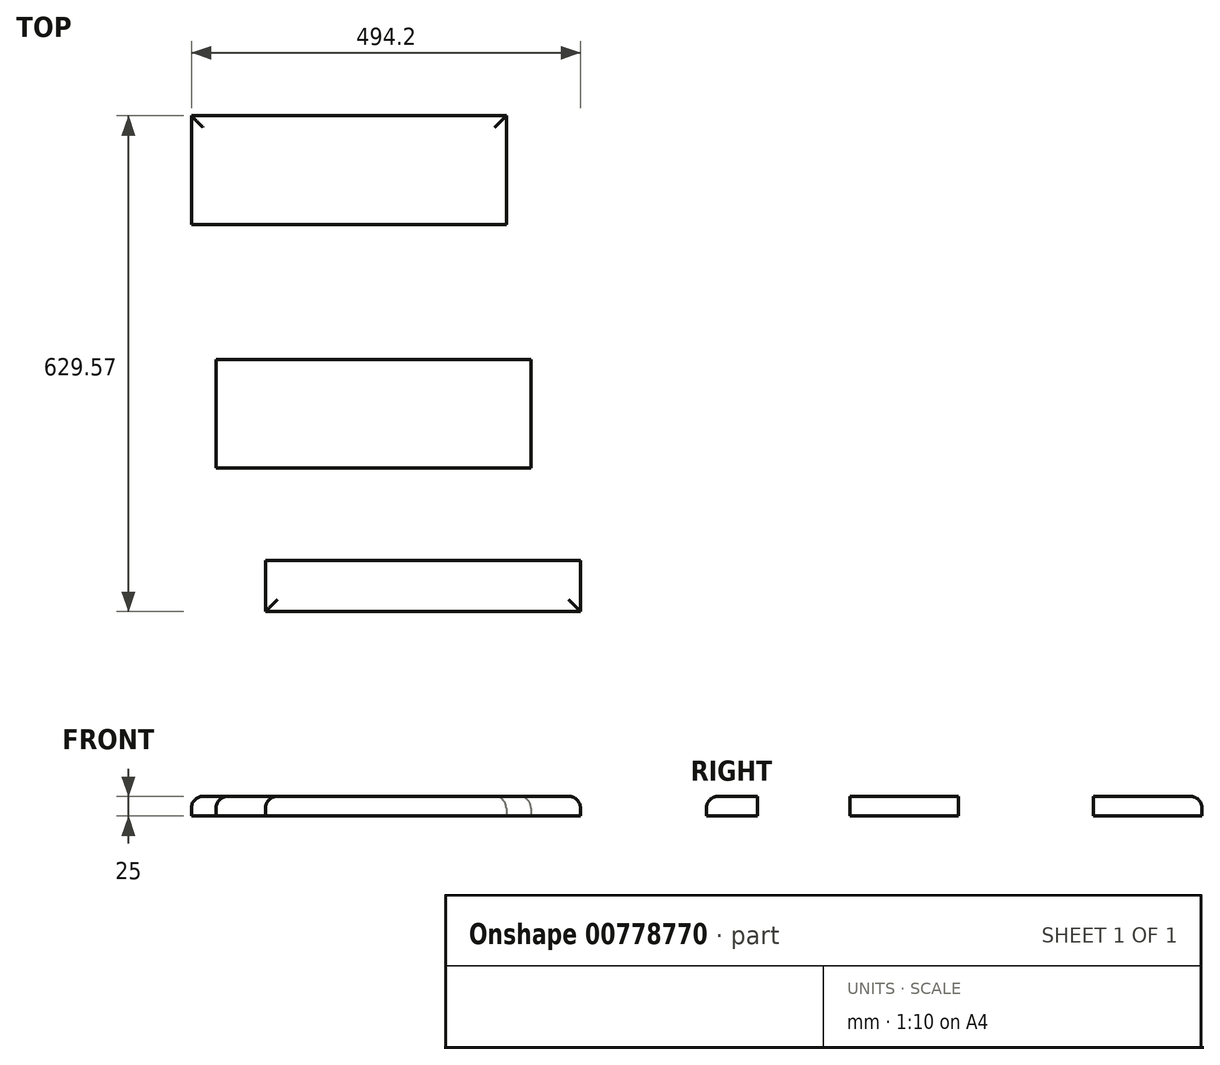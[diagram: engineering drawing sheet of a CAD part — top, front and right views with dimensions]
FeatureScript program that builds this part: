
annotation { "Feature Type Name" : "Feature", "Feature Type Description" : "" }
export const myFeature = defineFeature(function(context is Context, id is Id, definition is map)
    precondition{}
    {
        {
            var Q0;
            Q0=qCreatedBy(makeId("Top.planeOp"),FACE);
            var sketch = newSketch(context, id + "F0", { "sketchPlane" : qUnion([Q0])});
            skLineSegment(sketch, "E0.bottom", {"start": v(-192.82, -49.95) * mm, "end": v(207.18, -49.95) * mm});
            skLineSegment(sketch, "E0.top", {"start": v(-192.82, 88.05) * mm, "end": v(207.18, 88.05) * mm});
            skLineSegment(sketch, "E0.left", {"start": v(-192.82, -49.95) * mm, "end": v(-192.82, 88.05) * mm});
            skLineSegment(sketch, "E0.right", {"start": v(207.18, -49.95) * mm, "end": v(207.18, 88.05) * mm});
            skSolve(sketch);
        }
        {
            var Q0;
            Q0=qCreatedBy(makeId("Top.planeOp"),FACE);
            var sketch = newSketch(context, id + "F1", { "sketchPlane" : qUnion([Q0])});
            skLineSegment(sketch, "E1.bottom", {"start": v(-161.48, -221.5) * mm, "end": v(238.52, -221.5) * mm});
            skLineSegment(sketch, "E1.top", {"start": v(-161.48, -359.5) * mm, "end": v(238.52, -359.5) * mm});
            skLineSegment(sketch, "E1.left", {"start": v(-161.48, -221.5) * mm, "end": v(-161.48, -359.5) * mm});
            skLineSegment(sketch, "E1.right", {"start": v(238.52, -221.5) * mm, "end": v(238.52, -359.5) * mm});
            skSolve(sketch);
        }
        {
            var Q0;
            Q0=qCreatedBy(makeId("Top.planeOp"),FACE);
            var sketch = newSketch(context, id + "F2", { "sketchPlane" : qUnion([Q0])});
            skLineSegment(sketch, "E2.bottom", {"start": v(-98.62, -476.52) * mm, "end": v(301.38, -476.52) * mm});
            skLineSegment(sketch, "E2.top", {"start": v(-98.62, -541.52) * mm, "end": v(301.38, -541.52) * mm});
            skLineSegment(sketch, "E2.left", {"start": v(-98.62, -476.52) * mm, "end": v(-98.62, -541.52) * mm});
            skLineSegment(sketch, "E2.right", {"start": v(301.38, -476.52) * mm, "end": v(301.38, -541.52) * mm});
            skSolve(sketch);
        }
        {
            var Q0;
            Q0=makeQuery(id+"F0.imprint","IMPRINT",FACE,{"disambiguationData":[TD([[makeQuery(id+"F0.imprint","IMPRINT",EDGE,{"derivedFrom":sQuery(id+"F0.wireOp",EDGE,"E0.bottom")}),1.0]])]});
            var Q1;
            Q1=makeQuery(id+"F1.imprint","IMPRINT",FACE,{"disambiguationData":[TD([[makeQuery(id+"F1.imprint","IMPRINT",EDGE,{"derivedFrom":sQuery(id+"F1.wireOp",EDGE,"E1.bottom")}),-1.0]])]});
            var Q2;
            Q2=makeQuery(id+"F2.imprint","IMPRINT",FACE,{"disambiguationData":[TD([[makeQuery(id+"F2.imprint","IMPRINT",EDGE,{"derivedFrom":sQuery(id+"F2.wireOp",EDGE,"E2.bottom")}),-1.0]])]});
            extrude(context, id + "F3", {"entities" : qUnion([Q0, Q1, Q2]), "depth" : 25 * mm, "offsetDistance" : 25 * mm});
        }
        {
            var Q0;
            Q0=makeQuery(id+"F3.opExtrude","CAP_EDGE",EDGE,{"disambiguationData":[OSD([sQuery(id+"F2.wireOp",EDGE,"E2.top")])],"isStart":false});
            var Q1;
            Q1=makeQuery(id+"F3.opExtrude","CAP_EDGE",EDGE,{"disambiguationData":[OSD([sQuery(id+"F2.wireOp",EDGE,"E2.right")])],"isStart":false});
            var Q2;
            Q2=makeQuery(id+"F3.opExtrude","CAP_EDGE",EDGE,{"disambiguationData":[OSD([sQuery(id+"F2.wireOp",EDGE,"E2.left")])],"isStart":false});
            var Q3;
            Q3=makeQuery(id+"F3.opExtrude","CAP_EDGE",EDGE,{"disambiguationData":[OSD([sQuery(id+"F1.wireOp",EDGE,"E1.left")])],"isStart":false});
            var Q4;
            Q4=makeQuery(id+"F3.opExtrude","CAP_EDGE",EDGE,{"disambiguationData":[OSD([sQuery(id+"F1.wireOp",EDGE,"E1.right")])],"isStart":false});
            var Q5;
            Q5=makeQuery(id+"F3.opExtrude","CAP_EDGE",EDGE,{"disambiguationData":[OSD([sQuery(id+"F0.wireOp",EDGE,"E0.right")])],"isStart":false});
            var Q6;
            Q6=makeQuery(id+"F3.opExtrude","CAP_EDGE",EDGE,{"disambiguationData":[OSD([sQuery(id+"F0.wireOp",EDGE,"E0.left")])],"isStart":false});
            var Q7;
            Q7=makeQuery(id+"F3.opExtrude","CAP_EDGE",EDGE,{"disambiguationData":[OSD([sQuery(id+"F0.wireOp",EDGE,"E0.top")])],"isStart":false});
            fillet(context, id + "F4", {"entities" : qUnion([Q0, Q1, Q2, Q3, Q4, Q5, Q6, Q7]), "radius" : 15 * mm, "tangentPropagation" : true, "allowEdgeOverflow" : false});
        }
    });
